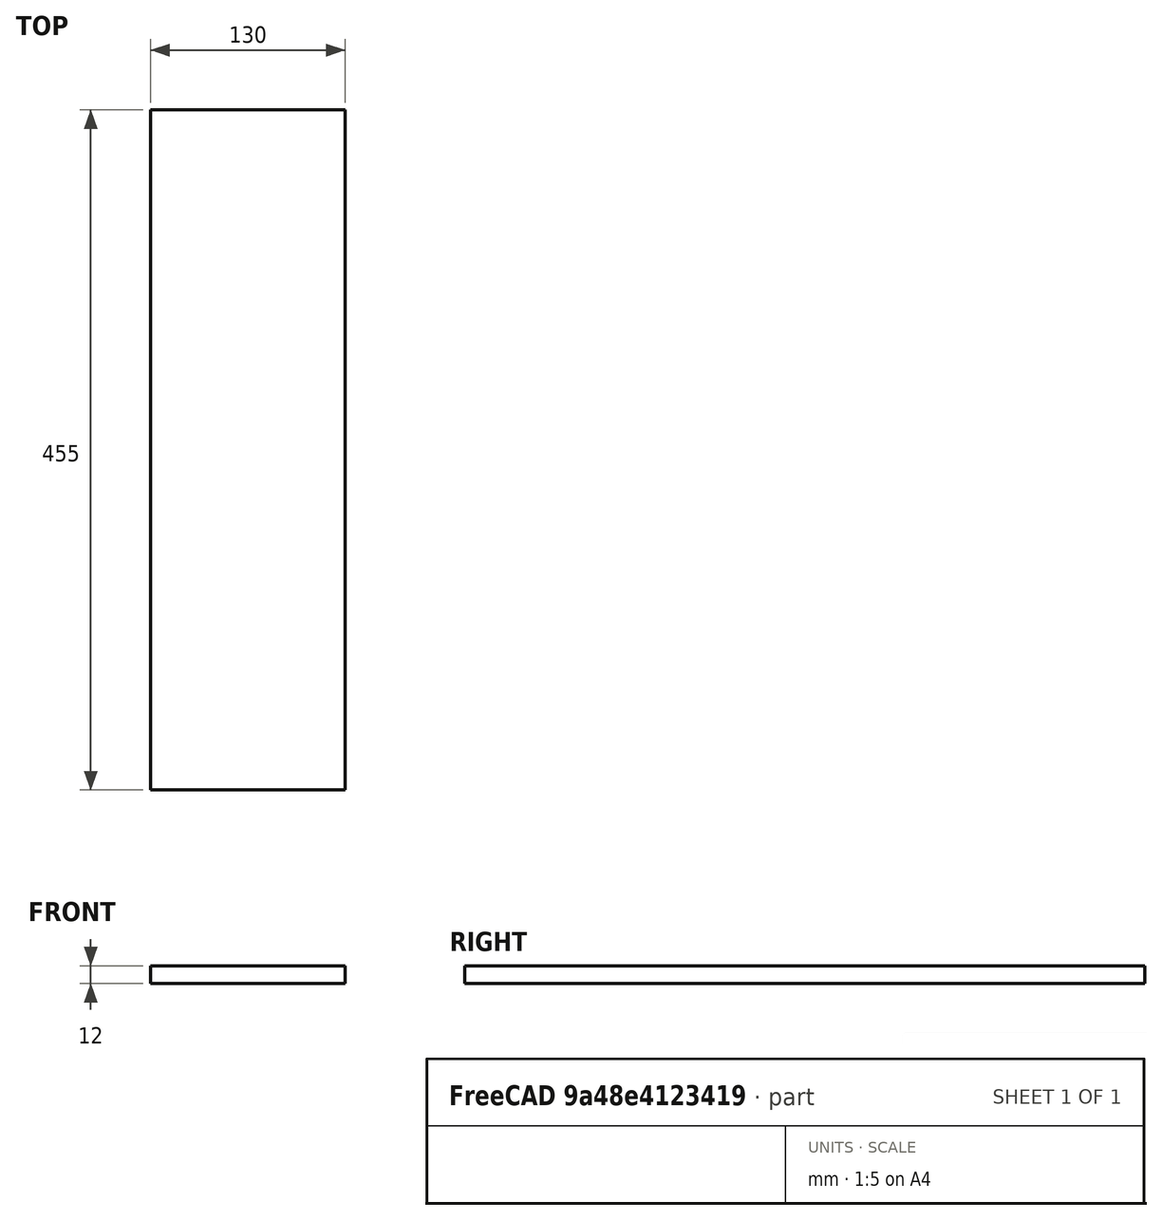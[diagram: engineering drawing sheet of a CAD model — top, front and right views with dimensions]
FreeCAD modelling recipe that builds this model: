
FCSTD DOCUMENT  (FreeCAD 0.19R24276 (Git))
Label: 1001_keyboard_floor_16_
License: All rights reserved
LicenseURL: http://en.wikipedia.org/wiki/All_rights_reserved
objects: Sketcher::SketchObject×1, PartDesign::Pad×1, PartDesign::Body×1, Spreadsheet::Sheet×1
note: 4 computed .brp shape members not serialized (recipe doc carries the construction recipe); baked Part::Feature solids carry a one-line shape summary decoded from their .brp

FEATURE [Sketcher::SketchObject] Sketch
  FullyConstrained = true
  MapMode = 5
  Support = -> [XY_Plane]
  expr: Constraints[6] = <<xls>>.k_d
  expr: Constraints[5] = <<xls>>.k_w
  sketch-geometry (5):
    g0: LineSegment StartX=0 StartY=455 StartZ=0 EndX=130 EndY=455 EndZ=0
    g1: LineSegment StartX=130 StartY=455 StartZ=0 EndX=130 EndY=0 EndZ=0
    g2: LineSegment StartX=130 StartY=0 StartZ=0 EndX=0 EndY=0 EndZ=0
    g3: LineSegment StartX=0 StartY=0 StartZ=0 EndX=0 EndY=227.5 EndZ=0
    g4: LineSegment StartX=0 StartY=227.5 StartZ=0 EndX=0 EndY=455 EndZ=0
  constraints (14):
    c: Coincident(g0,g1)
    c: Coincident(g1,g2)
    c: Horizontal(g0)
    c: Horizontal(g2)
    c: Vertical(g1)
    c: DistanceY(g1,g1) = 455
    c: DistanceX(g0,g0) = 130
    c: Coincident(g3,g2)
    c: Coincident(g4,g0)
    c: Equal(g3,g4)
    c: Vertical(g4)
    c: Vertical(g3)
    c: Coincident(g3,g4)
    c: Coincident(g2,g-1)
FEATURE [PartDesign::Pad] Pad
  AllowMultiFace = false
  Direction = (1,1,1)
  Length = 12
  Length2 = 100
  Profile = -> Sketch
  Type = 0
  expr: Length = <<xls>>.k_t_0
FEATURE [PartDesign::Body] Body
  Group = -> [Sketch,Pad]
  Origin = -> Origin
  Tip = -> Pad
FEATURE [Spreadsheet::Sheet] Spreadsheet  label="xls"
  cells = B1=INHERITED; C1=Sperrholz Birke Phenol 2-seitig glatt 12 mm; B2=Thickness Front; D2=12; E2=mm; B3=Width Cabinet Floor; D3=495; E3=mm; B5=FLOOR; C5=Sperrholz Birke 12 mm; B6=Thickness; C6=k_t_0; D6(k_t_0)=12; E6=mm; B7=Width Nominal; D7==D3; F7=Floor width; G7=strutt; H7=strutt; I7=tolerance; B8=Width; C8=k_w; D8(k_w)==D3 - G8 - H8 - I8; E8=mm; F8=495; G8=18; H8=18; I8=4; B9=Deapth Nominal; D9=150; B10=Deapth; C10=k_d; D10(k_d)=130; E10=mm
